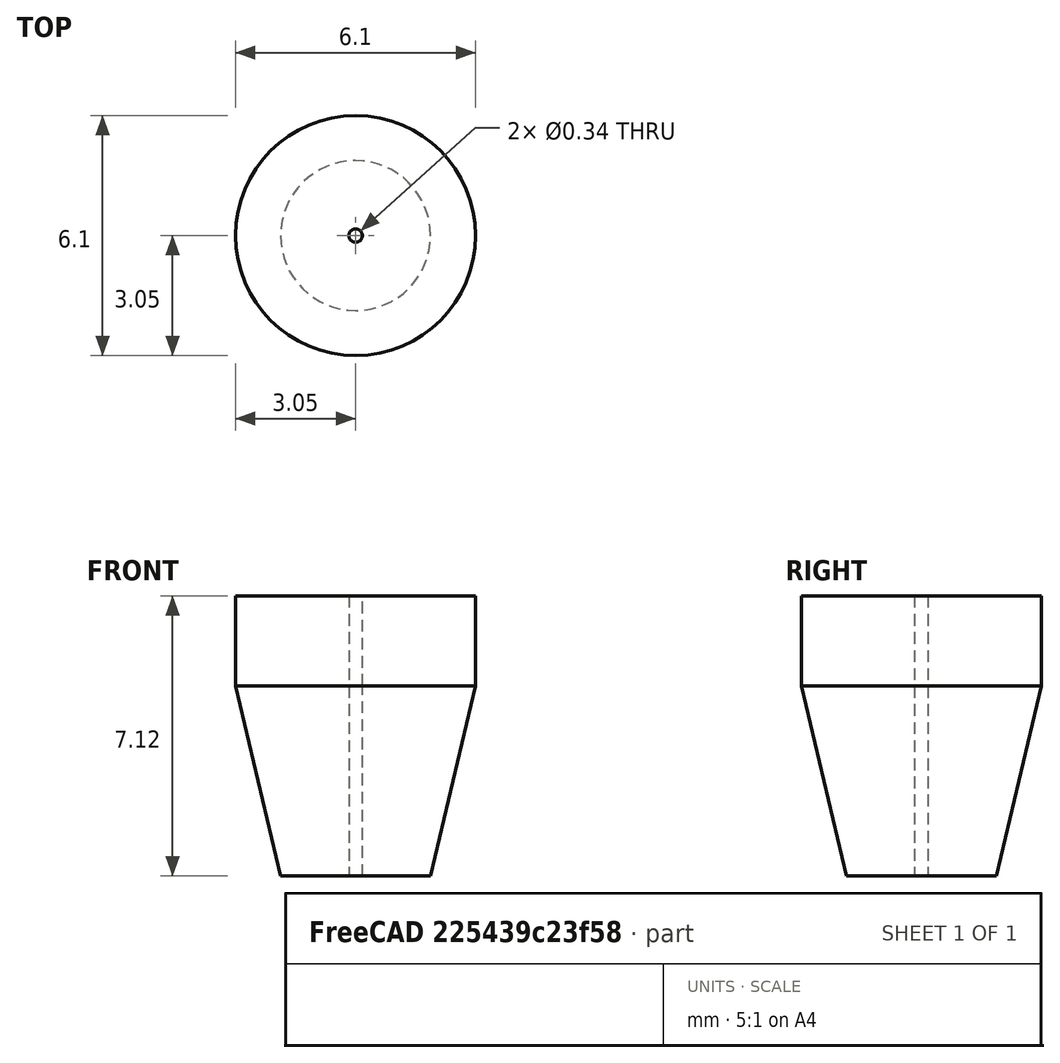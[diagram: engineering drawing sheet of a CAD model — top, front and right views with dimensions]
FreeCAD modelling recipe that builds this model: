
FCSTD DOCUMENT  (FreeCAD 0.21R0.21.2)
Label: FiberFerruleSingle
License: All rights reserved
LicenseURL: http://en.wikipedia.org/wiki/All_rights_reserved
objects: Part::Cylinder×2, Part::Cone×1, Part::MultiFuse×1, Part::Cut×1
note: 5 computed .brp shape members not serialized (recipe doc carries the construction recipe); baked Part::Feature solids carry a one-line shape summary decoded from their .brp

FEATURE [Part::Cone] Cone
  Angle = 360
  AttacherType = Attacher::AttachEngine3D
  Height = 4.826
  Radius1 = 1.905
  Radius2 = 3.048
FEATURE [Part::Cylinder] Cylinder
  Angle = 360
  AttacherType = Attacher::AttachEngine3D
  FirstAngle = 0
  Height = 2.286
  Placement = pos=(0,0,4.83) rot=(0,0,1;0rad)
  Radius = 3.05
  SecondAngle = 0
FEATURE [Part::MultiFuse] Fusion  label="SwagelokPTFEFerrule"
  Shapes = -> [Cone,Cylinder]
FEATURE [Part::Cylinder] Cylinder001  label="Fiber0"
  Angle = 360
  AttacherType = Attacher::AttachEngine3D
  FirstAngle = 0
  Height = 7.12
  Radius = 0.17145
  SecondAngle = 0
FEATURE [Part::Cut] Cut  label="SwagelokFiberFerruleSingle0.125in"
  Base = -> Fusion
  Tool = -> Cylinder001
